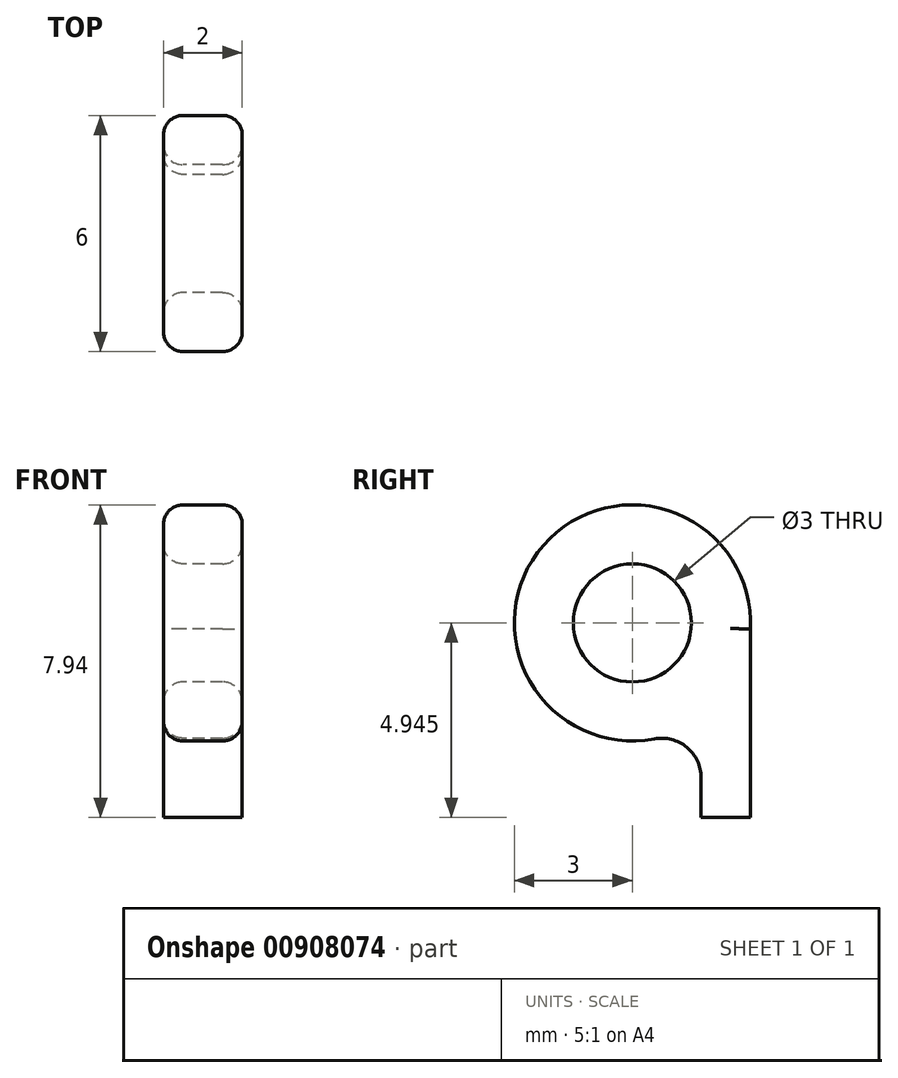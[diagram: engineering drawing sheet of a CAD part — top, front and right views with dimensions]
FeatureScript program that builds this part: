
annotation { "Feature Type Name" : "Feature", "Feature Type Description" : "" }
export const myFeature = defineFeature(function(context is Context, id is Id, definition is map)
    precondition{}
    {
        {
            var Q0;
            Q0=qCreatedBy(makeId("Right.planeOp"),FACE);
            var sketch = newSketch(context, id + "F0", { "sketchPlane" : qUnion([Q0])});
            skCircle(sketch, "E0", {"center": v(0, 0.15) * mm, "radius": 1.5 * mm});
            skArc(sketch, "E1.0", {"start": v(3, 0) * mm, "mid": v(-2.26, 2.13) * mm, "end": v(0.56, -2.8) * mm});
            skLineSegment(sketch, "E2", {"start": v(3, 0) * mm, "end": v(3, -4.8) * mm});
            skLineSegment(sketch, "E3", {"start": v(3, -4.8) * mm, "end": v(1.75, -4.8) * mm});
            skLineSegment(sketch, "E4", {"start": v(1.75, -4.8) * mm, "end": v(1.75, -3.77) * mm});
            skPoint(sketch, "E5.visualSharp", {"position": v(1.75, -2.28) * mm});
            skArc(sketch, "E5.filletArc", {"start": v(1.75, -3.77) * mm, "mid": v(1.38, -3) * mm, "end": v(0.56, -2.8) * mm});
            skSolve(sketch);
        }
        {
            var Q0;
            Q0=makeQuery(id+"F0.imprint","IMPRINT",FACE,{"disambiguationData":[TD([[makeQuery(id+"F0.imprint","IMPRINT",EDGE,{"derivedFrom":sQuery(id+"F0.wireOp",EDGE,"E0")}),-1.0]])]});
            extrude(context, id + "F1", {"entities" : qUnion([Q0]), "depth" : 2 * mm, "offsetDistance" : 25 * mm});
        }
        {
            var Q0;
            Q0=makeQuery(id+"F1.opExtrude","CAP_EDGE",EDGE,{"disambiguationData":[OSD([sQuery(id+"F0.wireOp",EDGE,"E1.0")])],"isStart":true});
            var Q1;
            Q1=makeQuery(id+"F1.opExtrude","CAP_EDGE",EDGE,{"disambiguationData":[OSD([sQuery(id+"F0.wireOp",EDGE,"E1.0")])],"isStart":false});
            var Q2;
            Q2=makeQuery(id+"F1.opExtrude","CAP_EDGE",EDGE,{"disambiguationData":[OSD([sQuery(id+"F0.wireOp",EDGE,"E0")])],"isStart":true});
            var Q3;
            Q3=makeQuery(id+"F1.opExtrude","CAP_EDGE",EDGE,{"disambiguationData":[OSD([sQuery(id+"F0.wireOp",EDGE,"E0")])],"isStart":false});
            fillet(context, id + "F2", {"entities" : qUnion([Q0, Q1, Q2, Q3]), "radius" : .5 * mm, "tangentPropagation" : true, "allowEdgeOverflow" : false});
        }
    });
